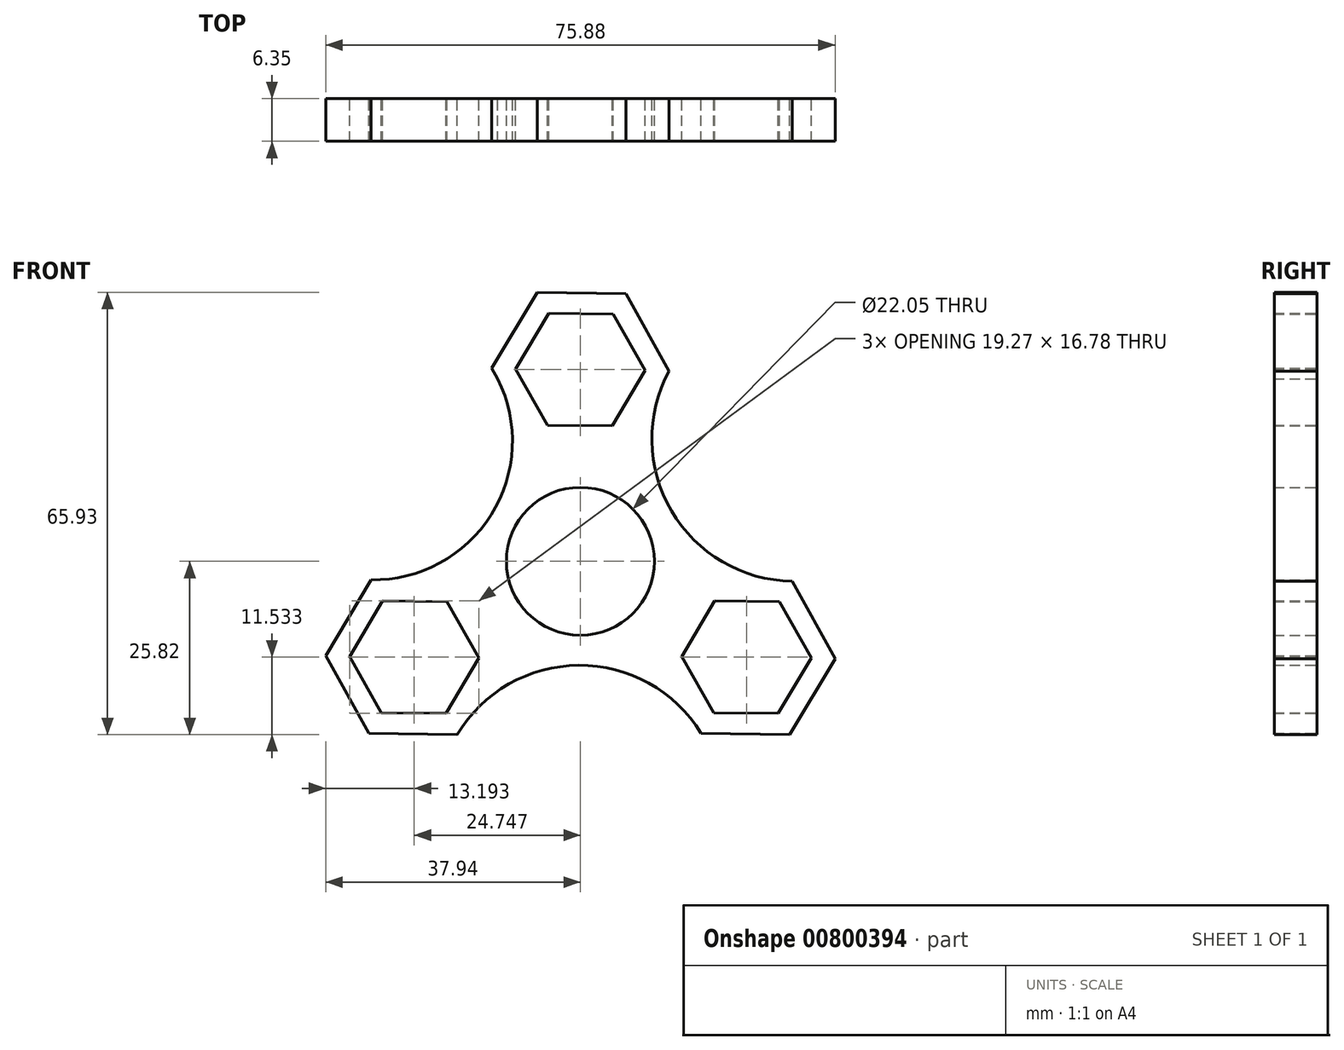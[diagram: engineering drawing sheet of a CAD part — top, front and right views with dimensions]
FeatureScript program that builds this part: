
annotation { "Feature Type Name" : "Feature", "Feature Type Description" : "" }
export const myFeature = defineFeature(function(context is Context, id is Id, definition is map)
    precondition{}
    {
        {
            var Q0;
            Q0=qCreatedBy(makeId("Front.planeOp"),FACE);
            var sketch = newSketch(context, id + "F0", { "sketchPlane" : qUnion([Q0])});
            skCircle(sketch, "E0", {"center": v(0, 0) * mm, "radius": 11.02 * mm});
            skCircle(sketch, "E1", {"center": v(0, 0) * mm, "radius": 14.29 * mm});
            skCircle(sketch, "E2.cCircle", {"center": v(0, 28.58) * mm, "radius": 8.34 * mm, "construction": true});
            skLineSegment(sketch, "E2.0", {"start": v(4.9, 36.87) * mm, "end": v(9.63, 28.48) * mm});
            skLineSegment(sketch, "E2.1", {"start": v(9.63, 28.48) * mm, "end": v(4.74, 20.19) * mm});
            skLineSegment(sketch, "E2.2", {"start": v(4.74, 20.19) * mm, "end": v(-4.9, 20.28) * mm});
            skLineSegment(sketch, "E2.3", {"start": v(-4.9, 20.28) * mm, "end": v(-9.63, 28.67) * mm});
            skLineSegment(sketch, "E2.4", {"start": v(-9.63, 28.67) * mm, "end": v(-4.74, 36.96) * mm});
            skLineSegment(sketch, "E2.5", {"start": v(-4.74, 36.96) * mm, "end": v(4.9, 36.87) * mm});
            skPoint(sketch, "E2.0.midPoint", {"position": v(7.27, 32.68) * mm});
            skCircle(sketch, "E3.cCircle", {"center": v(0, 28.58) * mm, "radius": 8.11 * mm, "construction": true});
            skLineSegment(sketch, "E3.0", {"start": v(-4.68, 36.69) * mm, "end": v(4.68, 36.69) * mm});
            skLineSegment(sketch, "E3.1", {"start": v(4.68, 36.69) * mm, "end": v(9.36, 28.57) * mm});
            skLineSegment(sketch, "E3.2", {"start": v(9.36, 28.57) * mm, "end": v(4.68, 20.46) * mm});
            skLineSegment(sketch, "E3.3", {"start": v(4.68, 20.46) * mm, "end": v(-4.68, 20.46) * mm});
            skLineSegment(sketch, "E3.4", {"start": v(-4.68, 20.46) * mm, "end": v(-9.36, 28.58) * mm});
            skLineSegment(sketch, "E3.5", {"start": v(-9.36, 28.58) * mm, "end": v(-4.68, 36.69) * mm});
            skPoint(sketch, "E3.0.midPoint", {"position": v(0, 36.69) * mm});
            skCircle(sketch, "E4.cCircle", {"center": v(0, 28.58) * mm, "radius": 11.43 * mm, "construction": true});
            skLineSegment(sketch, "E4.0", {"start": v(-13.2, 28.8) * mm, "end": v(-6.41, 40.11) * mm});
            skLineSegment(sketch, "E4.1", {"start": v(-6.41, 40.11) * mm, "end": v(6.78, 39.9) * mm});
            skLineSegment(sketch, "E4.2", {"start": v(6.78, 39.9) * mm, "end": v(13.2, 28.36) * mm});
            skLineSegment(sketch, "E4.3", {"start": v(13.2, 28.36) * mm, "end": v(6.41, 17.04) * mm});
            skLineSegment(sketch, "E4.4", {"start": v(6.41, 17.04) * mm, "end": v(-6.78, 17.25) * mm});
            skLineSegment(sketch, "E4.5", {"start": v(-6.78, 17.25) * mm, "end": v(-13.2, 28.8) * mm});
            skPoint(sketch, "E4.0.midPoint", {"position": v(-9.8, 34.45) * mm});
            skPoint(sketch, "E5.1.0", {"position": v(-24.93, -25.72) * mm});
            skLineSegment(sketch, "E5.1.1", {"start": v(-20.06, -6.18) * mm, "end": v(-15.38, -14.29) * mm});
            skCircle(sketch, "E5.1.2", {"center": v(-24.75, -14.29) * mm, "radius": 8.34 * mm, "construction": true});
            skLineSegment(sketch, "E5.1.3", {"start": v(-18.33, -25.82) * mm, "end": v(-31.53, -25.6) * mm});
            skLineSegment(sketch, "E5.1.4", {"start": v(-31.16, -2.75) * mm, "end": v(-17.96, -2.97) * mm});
            skLineSegment(sketch, "E5.1.5", {"start": v(-29.48, -5.9) * mm, "end": v(-19.85, -5.99) * mm});
            skPoint(sketch, "E5.1.7", {"position": v(-31.93, -10.05) * mm});
            skLineSegment(sketch, "E5.1.8", {"start": v(-31.53, -25.6) * mm, "end": v(-37.94, -14.07) * mm});
            skPoint(sketch, "E5.1.10", {"position": v(-31.77, -18.34) * mm});
            skLineSegment(sketch, "E5.1.11", {"start": v(-37.94, -14.07) * mm, "end": v(-31.16, -2.75) * mm});
            skLineSegment(sketch, "E5.1.12", {"start": v(-17.96, -2.97) * mm, "end": v(-11.55, -14.5) * mm});
            skCircle(sketch, "E5.1.13", {"center": v(-24.75, -14.29) * mm, "radius": 11.43 * mm, "construction": true});
            skLineSegment(sketch, "E5.1.14", {"start": v(-11.55, -14.5) * mm, "end": v(-18.33, -25.82) * mm});
            skLineSegment(sketch, "E5.1.15", {"start": v(-20, -22.68) * mm, "end": v(-29.64, -22.59) * mm});
            skCircle(sketch, "E5.1.16", {"center": v(-24.75, -14.29) * mm, "radius": 8.11 * mm, "construction": true});
            skLineSegment(sketch, "E5.1.17", {"start": v(-34.38, -14.2) * mm, "end": v(-29.48, -5.9) * mm});
            skLineSegment(sketch, "E5.1.18", {"start": v(-19.85, -5.99) * mm, "end": v(-15.11, -14.38) * mm});
            skLineSegment(sketch, "E5.1.19", {"start": v(-15.38, -14.29) * mm, "end": v(-20.06, -22.4) * mm});
            skLineSegment(sketch, "E5.1.20", {"start": v(-15.11, -14.38) * mm, "end": v(-20, -22.68) * mm});
            skLineSegment(sketch, "E5.1.21", {"start": v(-29.43, -22.4) * mm, "end": v(-34.11, -14.29) * mm});
            skLineSegment(sketch, "E5.1.22", {"start": v(-20.06, -22.4) * mm, "end": v(-29.43, -22.4) * mm});
            skLineSegment(sketch, "E5.1.23", {"start": v(-29.64, -22.59) * mm, "end": v(-34.38, -14.2) * mm});
            skLineSegment(sketch, "E5.1.24", {"start": v(-34.11, -14.29) * mm, "end": v(-29.43, -6.18) * mm});
            skLineSegment(sketch, "E5.1.25", {"start": v(-29.43, -6.18) * mm, "end": v(-20.06, -6.18) * mm});
            skPoint(sketch, "E5.2.0", {"position": v(34.74, -8.73) * mm});
            skLineSegment(sketch, "E5.2.1", {"start": v(15.38, -14.29) * mm, "end": v(20.06, -6.18) * mm});
            skCircle(sketch, "E5.2.2", {"center": v(24.75, -14.29) * mm, "radius": 8.34 * mm, "construction": true});
            skLineSegment(sketch, "E5.2.3", {"start": v(31.53, -2.97) * mm, "end": v(37.94, -14.5) * mm});
            skLineSegment(sketch, "E5.2.4", {"start": v(17.96, -25.6) * mm, "end": v(11.55, -14.07) * mm});
            skLineSegment(sketch, "E5.2.5", {"start": v(19.85, -22.59) * mm, "end": v(15.11, -14.2) * mm});
            skPoint(sketch, "E5.2.7", {"position": v(24.67, -22.63) * mm});
            skLineSegment(sketch, "E5.2.8", {"start": v(37.94, -14.5) * mm, "end": v(31.16, -25.82) * mm});
            skPoint(sketch, "E5.2.10", {"position": v(31.77, -18.34) * mm});
            skLineSegment(sketch, "E5.2.11", {"start": v(31.16, -25.82) * mm, "end": v(17.96, -25.6) * mm});
            skLineSegment(sketch, "E5.2.12", {"start": v(11.55, -14.07) * mm, "end": v(18.33, -2.75) * mm});
            skCircle(sketch, "E5.2.13", {"center": v(24.75, -14.29) * mm, "radius": 11.43 * mm, "construction": true});
            skLineSegment(sketch, "E5.2.14", {"start": v(18.33, -2.75) * mm, "end": v(31.53, -2.97) * mm});
            skLineSegment(sketch, "E5.2.15", {"start": v(29.64, -5.99) * mm, "end": v(34.38, -14.38) * mm});
            skCircle(sketch, "E5.2.16", {"center": v(24.75, -14.29) * mm, "radius": 8.11 * mm, "construction": true});
            skLineSegment(sketch, "E5.2.17", {"start": v(29.48, -22.68) * mm, "end": v(19.85, -22.59) * mm});
            skLineSegment(sketch, "E5.2.18", {"start": v(15.11, -14.2) * mm, "end": v(20, -5.9) * mm});
            skLineSegment(sketch, "E5.2.19", {"start": v(20.06, -6.18) * mm, "end": v(29.43, -6.18) * mm});
            skLineSegment(sketch, "E5.2.20", {"start": v(20, -5.9) * mm, "end": v(29.64, -5.99) * mm});
            skLineSegment(sketch, "E5.2.21", {"start": v(34.11, -14.29) * mm, "end": v(29.43, -22.4) * mm});
            skLineSegment(sketch, "E5.2.22", {"start": v(29.43, -6.18) * mm, "end": v(34.11, -14.29) * mm});
            skLineSegment(sketch, "E5.2.23", {"start": v(34.38, -14.38) * mm, "end": v(29.48, -22.68) * mm});
            skLineSegment(sketch, "E5.2.24", {"start": v(29.43, -22.4) * mm, "end": v(20.06, -22.4) * mm});
            skLineSegment(sketch, "E5.2.25", {"start": v(20.06, -22.4) * mm, "end": v(15.38, -14.29) * mm});
            skArc(sketch, "E6", {"start": v(-31.16, -2.75) * mm, "mid": v(-12.84, 7.7) * mm, "end": v(-13.2, 28.8) * mm});
            skArc(sketch, "E7", {"start": v(17.96, -25.6) * mm, "mid": v(-0.25, -15.5) * mm, "end": v(-18.33, -25.82) * mm});
            skArc(sketch, "E8", {"start": v(13.2, 28.36) * mm, "mid": v(13.55, 7.54) * mm, "end": v(31.53, -2.97) * mm});
            skSolve(sketch);
        }
        {
            var Q0;
            Q0 = qSketchRegion(id + "F0", true);
            var Q1;
            Q1=makeQuery(id+"F0.imprint","IMPRINT",FACE,{"disambiguationData":[TD([[makeQuery(id+"F0.imprint","IMPRINT",EDGE,{"derivedFrom":sQuery(id+"F0.wireOp",EDGE,"E1")}),1.0]])]});
            extrude(context, id + "F1", {"entities" : qUnion([Q0, Q1]), "depth" : 25.4 * mm, "offsetDistance" : 25.4 * mm});
        }
        {
            var Q0;
            Q0=makeQuery(id+"F1.opExtrude","CAP_FACE",FACE,{"disambiguationData":[OSD([sQuery(id+"F0.wireOp",EDGE,"E2.0"),sQuery(id+"F0.wireOp",EDGE,"E2.1"),sQuery(id+"F0.wireOp",EDGE,"E2.2"),sQuery(id+"F0.wireOp",EDGE,"E2.3"),sQuery(id+"F0.wireOp",EDGE,"E2.4"),sQuery(id+"F0.wireOp",EDGE,"E2.5"),sQuery(id+"F0.wireOp",EDGE,"E4.0"),sQuery(id+"F0.wireOp",EDGE,"E4.1"),sQuery(id+"F0.wireOp",EDGE,"E4.2"),sQuery(id+"F0.wireOp",EDGE,"E4.5"),sQuery(id+"F0.wireOp",EDGE,"E5.1.3"),sQuery(id+"F0.wireOp",EDGE,"E5.1.5"),sQuery(id+"F0.wireOp",EDGE,"E5.1.8"),sQuery(id+"F0.wireOp",EDGE,"E5.1.11"),sQuery(id+"F0.wireOp",EDGE,"E5.1.15"),sQuery(id+"F0.wireOp",EDGE,"E5.1.17"),sQuery(id+"F0.wireOp",EDGE,"E5.1.18"),sQuery(id+"F0.wireOp",EDGE,"E5.1.20"),sQuery(id+"F0.wireOp",EDGE,"E5.1.23"),sQuery(id+"F0.wireOp",EDGE,"E5.2.3"),sQuery(id+"F0.wireOp",EDGE,"E5.2.5"),sQuery(id+"F0.wireOp",EDGE,"E5.2.8"),sQuery(id+"F0.wireOp",EDGE,"E0"),sQuery(id+"F0.wireOp",EDGE,"E5.2.11"),sQuery(id+"F0.wireOp",EDGE,"E5.2.15"),sQuery(id+"F0.wireOp",EDGE,"E5.2.17"),sQuery(id+"F0.wireOp",EDGE,"E5.2.18"),sQuery(id+"F0.wireOp",EDGE,"E5.2.20"),sQuery(id+"F0.wireOp",EDGE,"E5.2.23"),sQuery(id+"F0.wireOp",EDGE,"E6"),sQuery(id+"F0.wireOp",EDGE,"E7"),sQuery(id+"F0.wireOp",EDGE,"E8")])],"isStart":false});
            extrude(context, id + "F2", {"entities" : qUnion([Q0]), "operationType" : NewBodyOperationType.REMOVE, "oppositeDirection" : true, "depth" : 19.05 * mm, "offsetDistance" : 25.4 * mm});
        }
    });
